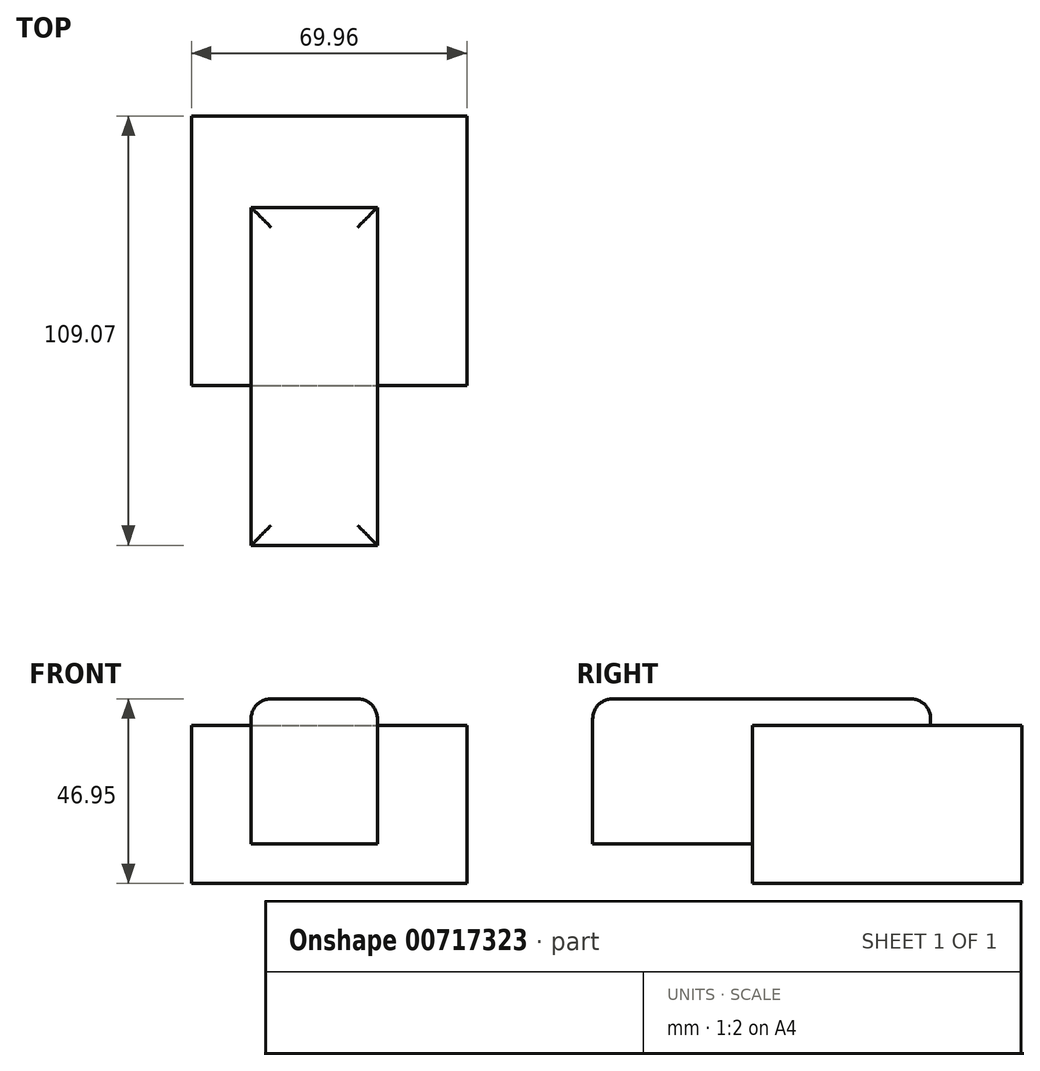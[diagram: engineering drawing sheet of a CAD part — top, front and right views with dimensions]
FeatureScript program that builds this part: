
annotation { "Feature Type Name" : "Feature", "Feature Type Description" : "" }
export const myFeature = defineFeature(function(context is Context, id is Id, definition is map)
    precondition{}
    {
        {
            var Q0;
            Q0=qCreatedBy(makeId("Top.planeOp"),FACE);
            var sketch = newSketch(context, id + "F0", { "sketchPlane" : qUnion([Q0])});
            skLineSegment(sketch, "E0.bottom", {"start": v(-29.5, -45.3) * mm, "end": v(40.47, -45.3) * mm});
            skLineSegment(sketch, "E0.top", {"start": v(-29.5, 23.22) * mm, "end": v(40.47, 23.22) * mm});
            skLineSegment(sketch, "E0.left", {"start": v(-29.5, -45.3) * mm, "end": v(-29.5, 23.22) * mm});
            skLineSegment(sketch, "E0.right", {"start": v(40.47, -45.3) * mm, "end": v(40.47, 23.22) * mm});
            skSolve(sketch);
        }
        {
            var Q0;
            Q0=makeQuery(id+"F0.imprint","IMPRINT",FACE,{"disambiguationData":[TD([[makeQuery(id+"F0.imprint","IMPRINT",EDGE,{"derivedFrom":sQuery(id+"F0.wireOp",EDGE,"E0.bottom")}),1.0]])]});
            extrude(context, id + "F1", {"entities" : qUnion([Q0]), "depth" : 40.13 * mm, "offsetDistance" : 25.4 * mm});
        }
        {
            var Q0;
            Q0=qCreatedBy(makeId("Front.planeOp"),FACE);
            var sketch = newSketch(context, id + "F2", { "sketchPlane" : qUnion([Q0])});
            skLineSegment(sketch, "E1.bottom", {"start": v(-14.33, 10.04) * mm, "end": v(17.77, 10.04) * mm});
            skLineSegment(sketch, "E1.top", {"start": v(-14.33, 46.95) * mm, "end": v(17.77, 46.95) * mm});
            skLineSegment(sketch, "E1.left", {"start": v(-14.33, 10.04) * mm, "end": v(-14.33, 46.95) * mm});
            skLineSegment(sketch, "E1.right", {"start": v(17.77, 10.04) * mm, "end": v(17.77, 46.95) * mm});
            skSolve(sketch);
        }
        {
            var Q0;
            Q0=makeQuery(id+"F2.imprint","IMPRINT",FACE,{"disambiguationData":[TD([[makeQuery(id+"F2.imprint","IMPRINT",EDGE,{"derivedFrom":sQuery(id+"F2.wireOp",EDGE,"E1.bottom")}),1.0]])]});
            extrude(context, id + "F3", {"entities" : qUnion([Q0]), "operationType" : NewBodyOperationType.ADD, "depth" : 85.85 * mm, "offsetDistance" : 25.4 * mm});
        }
        {
            var Q0;
            Q0=makeQuery(id+"F3.opExtrude","SWEPT_FACE",FACE,{"disambiguationData":[OSD([sQuery(id+"F2.wireOp",EDGE,"E1.top")])]});
            fillet(context, id + "F4", {"entities" : qUnion([Q0]), "radius" : 5.08 * mm, "tangentPropagation" : true, "allowEdgeOverflow" : false});
        }
    });
